# Revit family: 6 inch PS Lintel -150W x 65H-mm
name_source: partatom
category: Generic Models
units: mm (PartAtom-declared; Revit-internal decimal feet)

## family parameters
Always vertical = Yes
Can host rebar = No
Cut with Voids When Loaded = No
Part Type = Normal
Room Calculation Point = No
Round Connector Dimension = Use Diameter
Shared = No
Work Plane-Based = No

## types (1)
- 6 inch PS Lintel -150W x 65H-mm
    Bearing Required = 150mm each end for an ope up to 1500mm, 225mm each end for opes exceeding 1500mm
    Characteristics Deflection Under Load = Not to exceed 1/200 across the length of each individual unit supplied.
    Compressive Strength of Concrete = 40N/mm²
    Concrete Class = C30/37 as per EN: 206-1:2002
    Construction Tolerance Class = I.S. EN 845-2:2013
    Construction Type = Precast
    Default Elevation = 0 mm  [stored 0 ft]
    Description = 150W x 65H Pre-stressed Lintel
    Detailing = As per design specification and product drawings.
    Dimension Accuracy Class = I.S. EN 845-2:2013
    Durability against Corrosion = Ref: EN:845-2:2013 Annex C Table C.3. Class 2 B without rendering. Class 2 A when rendered.
    Keynote = The information contained is the sole property of KPC Ltd., any reproduction in part or whole without permission of KPC Ltd. is prohibited.
    Length Options = Stock sizes 609mm, 762mm, 914mm, 1066mm, 1219mm, 1371mm, 1524mm, 1676mm, 1828mm, 1981mm, 2133mm, 2286mm, 2438mm, 2590mm, 2743mm 2895mm, 3048mm, 3200mm, 3352mm, 3505mm, 3657mm, 3809mm, 3962mm
    Load Bearing = Yes
    Manufacturer = Killeshal Precast Concrete Ltd.
    Model = L/280 Concrete Lintel
    Nominal Cover to Main Bar = 32.5mm
    Resistance to Fire = Subject to nature of associated and or adjoining construction.
    Service Life = 0.000000
    Shape = Rectangular
    Size = 150mm x 65mm
    Slope = 0.00°
    Span = Lintel Length
    Type Comments = Visit our website for a full list of available products.
    Types = Single
    URL = www.killeshal.com
    Weight = 24Kg/m

note: [stored X ft] marks values corroborated as IEEE doubles in the binary element streams (Revit-internal decimal feet)

## geometry (parser evidence)
native form markers: Sweep x3
no freeform markers — native parametric forms only
